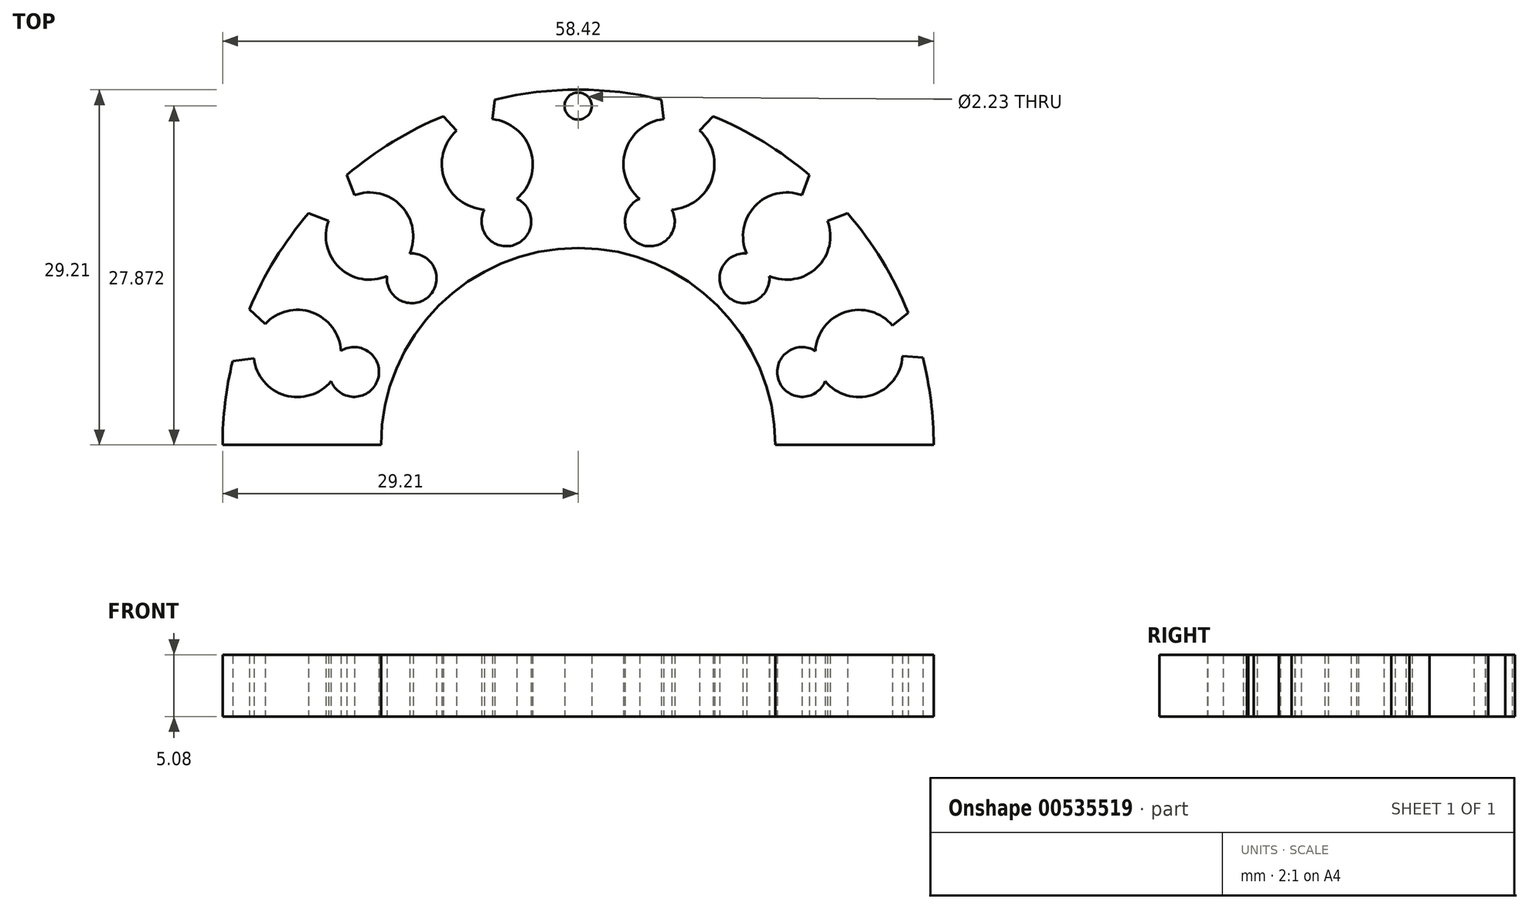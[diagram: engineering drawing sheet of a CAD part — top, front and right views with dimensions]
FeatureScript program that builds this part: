
annotation { "Feature Type Name" : "Feature", "Feature Type Description" : "" }
export const myFeature = defineFeature(function(context is Context, id is Id, definition is map)
    precondition{}
    {
        {
            var Q0;
            Q0=qCreatedBy(makeId("Top.planeOp"),FACE);
            var sketch = newSketch(context, id + "F0", { "sketchPlane" : qUnion([Q0])});
            skArc(sketch, "E0", {"start": v(16.2, 0) * mm, "mid": v(0, 16.2) * mm, "end": v(-16.2, 0) * mm});
            skArc(sketch, "E1", {"start": v(-9.99, 25.84) * mm, "mid": v(-10.99, 21.84) * mm, "end": v(-7.7, 19.36) * mm});
            skArc(sketch, "E2", {"start": v(-20.5, 18.43) * mm, "mid": v(-19.6, 14.58) * mm, "end": v(-15.7, 13.89) * mm});
            skArc(sketch, "E3", {"start": v(-26.63, 7.1) * mm, "mid": v(-24.09, 4.08) * mm, "end": v(-20.3, 5.24) * mm});
            skArc(sketch, "E4", {"start": v(-20.3, 5.24) * mm, "mid": v(-16.46, 5.37) * mm, "end": v(-19.49, 7.73) * mm});
            skArc(sketch, "E5", {"start": v(-15.7, 13.89) * mm, "mid": v(-12.23, 12.26) * mm, "end": v(-13.85, 15.74) * mm});
            skArc(sketch, "E6", {"start": v(-7.7, 19.36) * mm, "mid": v(-5.25, 16.45) * mm, "end": v(-5.04, 20.24) * mm});
            skLineSegment(sketch, "E7", {"start": v(-29.21, 0) * mm, "end": v(-16.2, 0) * mm});
            skArc(sketch, "E8.MirrorC", {"start": v(9.99, 25.84) * mm, "mid": v(10.99, 21.84) * mm, "end": v(7.7, 19.36) * mm});
            skArc(sketch, "E9.MirrorC", {"start": v(7.7, 19.36) * mm, "mid": v(5.25, 16.45) * mm, "end": v(5.04, 20.24) * mm});
            skArc(sketch, "E10.MirrorC", {"start": v(15.7, 13.89) * mm, "mid": v(12.23, 12.26) * mm, "end": v(13.85, 15.74) * mm});
            skArc(sketch, "E11.MirrorC", {"start": v(20.5, 18.43) * mm, "mid": v(19.6, 14.58) * mm, "end": v(15.7, 13.89) * mm});
            skArc(sketch, "E12.MirrorC", {"start": v(20.3, 5.24) * mm, "mid": v(16.46, 5.37) * mm, "end": v(19.49, 7.73) * mm});
            skArc(sketch, "E13.MirrorC", {"start": v(26.65, 7.3) * mm, "mid": v(24.18, 4.1) * mm, "end": v(20.3, 5.24) * mm});
            skCircle(sketch, "E14", {"center": v(0, 27.87) * mm, "radius": 1.11 * mm});
            skArc(sketch, "E15", {"start": v(29.21, 0) * mm, "mid": v(28.99, 3.63) * mm, "end": v(28.32, 7.2) * mm});
            skLineSegment(sketch, "E16.MirrorCS", {"start": v(-17.22, -23.6) * mm, "end": v(-18.24, -25) * mm});
            skLineSegment(sketch, "E17.MirrorCS", {"start": v(25.83, 9.81) * mm, "end": v(27.12, 10.88) * mm});
            skLineSegment(sketch, "E18.MirrorCS", {"start": v(26.65, 7.3) * mm, "end": v(28.32, 7.2) * mm});
            skLineSegment(sketch, "E19", {"start": v(-7.03, 26.8) * mm, "end": v(-6.84, 28.4) * mm});
            skLineSegment(sketch, "E20", {"start": v(-18.39, 20.54) * mm, "end": v(-19, 22.2) * mm});
            skLineSegment(sketch, "E21", {"start": v(-25.7, 9.95) * mm, "end": v(-27, 11.15) * mm});
            skLineSegment(sketch, "E22.MirrorCS", {"start": v(-26.63, 7.1) * mm, "end": v(-28.39, 6.9) * mm});
            skLineSegment(sketch, "E23.MirrorCS", {"start": v(-20.5, 18.43) * mm, "end": v(-22.15, 19.05) * mm});
            skLineSegment(sketch, "E24.MirrorCS", {"start": v(-9.99, 25.84) * mm, "end": v(-11.08, 27.03) * mm});
            skLineSegment(sketch, "E25.MirrorCS", {"start": v(9.99, 25.84) * mm, "end": v(11.08, 27.03) * mm});
            skLineSegment(sketch, "E26.MirrorCS", {"start": v(7.03, 26.8) * mm, "end": v(6.84, 28.4) * mm});
            skLineSegment(sketch, "E27.MirrorCS", {"start": v(18.39, 20.54) * mm, "end": v(19, 22.2) * mm});
            skLineSegment(sketch, "E28.MirrorCS", {"start": v(20.5, 18.43) * mm, "end": v(22.15, 19.05) * mm});
            skLineSegment(sketch, "E29.trimOffspring", {"start": v(16.2, 0) * mm, "end": v(29.21, 0) * mm});
            skArc(sketch, "E30.trimOffspring", {"start": v(-28.39, 6.9) * mm, "mid": v(-29, 3.48) * mm, "end": v(-29.21, 0) * mm});
            skArc(sketch, "E31.trimOffspring", {"start": v(-19.49, 7.73) * mm, "mid": v(-21.86, 10.9) * mm, "end": v(-25.7, 9.95) * mm});
            skArc(sketch, "E32.trimOffspring", {"start": v(-22.15, 19.05) * mm, "mid": v(-24.9, 15.3) * mm, "end": v(-27, 11.15) * mm});
            skArc(sketch, "E33.trimOffspring", {"start": v(-13.85, 15.74) * mm, "mid": v(-14.53, 19.64) * mm, "end": v(-18.39, 20.54) * mm});
            skArc(sketch, "E34.trimOffspring", {"start": v(-11.08, 27.03) * mm, "mid": v(-15.23, 24.93) * mm, "end": v(-19, 22.2) * mm});
            skArc(sketch, "E35.trimOffspring", {"start": v(-5.04, 20.24) * mm, "mid": v(-3.89, 24.17) * mm, "end": v(-7.03, 26.8) * mm});
            skArc(sketch, "E36.trimOffspring", {"start": v(6.84, 28.4) * mm, "mid": v(0, 29.21) * mm, "end": v(-6.84, 28.4) * mm});
            skArc(sketch, "E37.trimOffspring", {"start": v(5.04, 20.24) * mm, "mid": v(3.89, 24.17) * mm, "end": v(7.03, 26.8) * mm});
            skArc(sketch, "E38.trimOffspring", {"start": v(19, 22.2) * mm, "mid": v(15.23, 24.93) * mm, "end": v(11.08, 27.03) * mm});
            skArc(sketch, "E39.trimOffspring", {"start": v(13.85, 15.74) * mm, "mid": v(14.53, 19.64) * mm, "end": v(18.39, 20.54) * mm});
            skArc(sketch, "E40.trimOffspring", {"start": v(27.12, 10.88) * mm, "mid": v(24.97, 15.17) * mm, "end": v(22.15, 19.05) * mm});
            skArc(sketch, "E41.trimOffspring", {"start": v(19.49, 7.73) * mm, "mid": v(21.95, 10.93) * mm, "end": v(25.83, 9.81) * mm});
            skPoint(sketch, "E42.orphan", {"position": v(-29.93, 0) * mm});
            skSolve(sketch);
        }
        {
            var Q0;
            Q0 = qSketchRegion(id + "F0", true);
            extrude(context, id + "F1", {"entities" : qUnion([Q0]), "depth" : 5.08 * mm, "offsetDistance" : 25.4 * mm});
        }
    });
